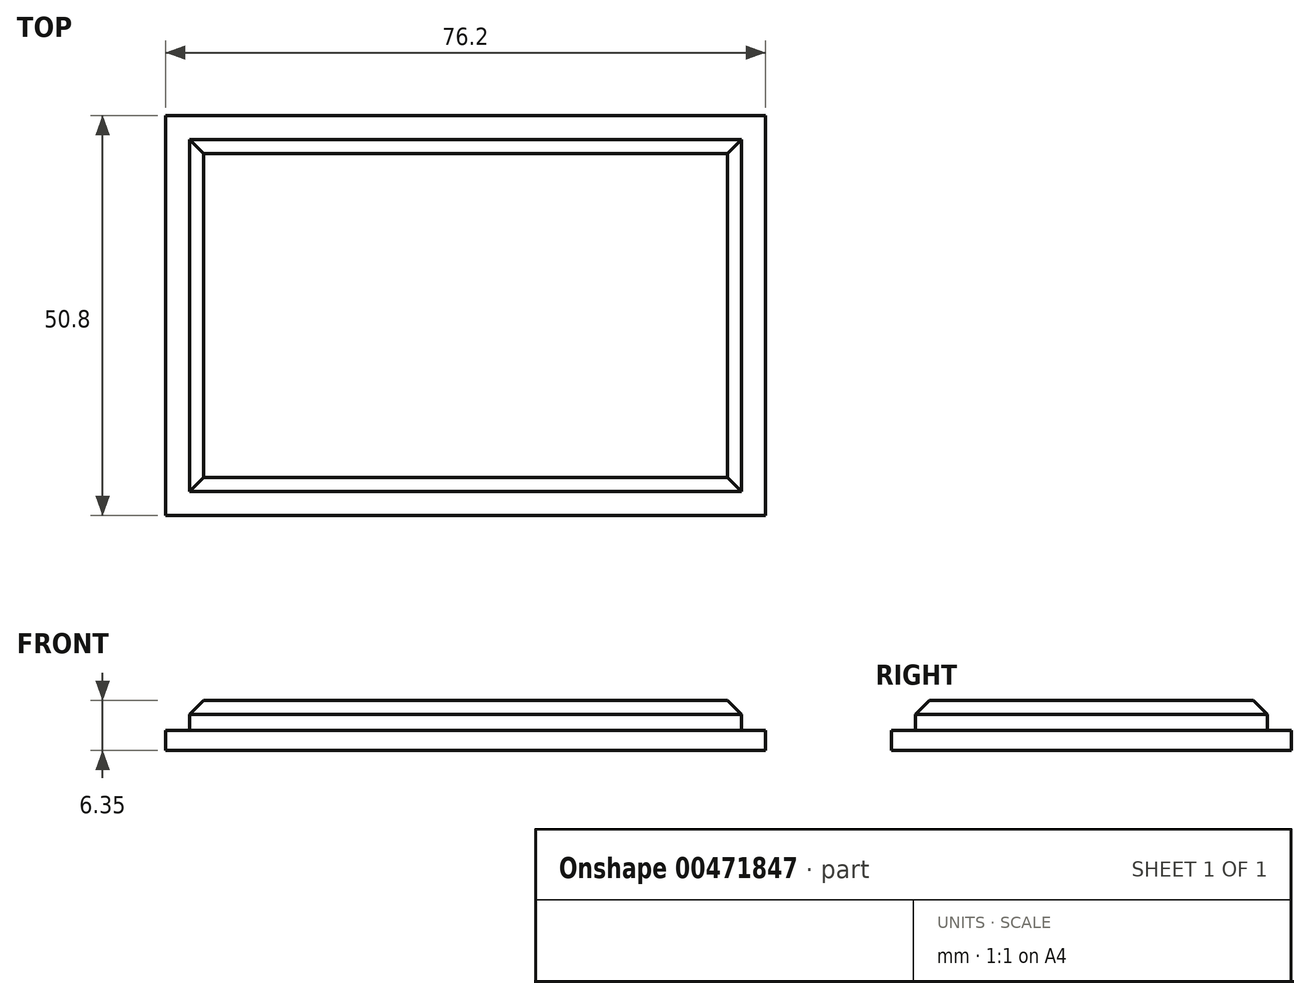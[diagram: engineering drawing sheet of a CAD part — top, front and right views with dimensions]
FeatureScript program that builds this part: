
annotation { "Feature Type Name" : "Feature", "Feature Type Description" : "" }
export const myFeature = defineFeature(function(context is Context, id is Id, definition is map)
    precondition{}
    {
        {
            var Q0;
            Q0=qCreatedBy(makeId("Top.planeOp"),FACE);
            var sketch = newSketch(context, id + "F0", { "sketchPlane" : qUnion([Q0])});
            skLineSegment(sketch, "E0.bottom", {"start": v(-35.2, 23.13) * mm, "end": v(41, 23.13) * mm});
            skLineSegment(sketch, "E0.top", {"start": v(-35.2, -27.67) * mm, "end": v(41, -27.67) * mm});
            skLineSegment(sketch, "E0.left", {"start": v(-35.2, 23.13) * mm, "end": v(-35.2, -27.67) * mm});
            skLineSegment(sketch, "E0.right", {"start": v(41, 23.13) * mm, "end": v(41, -27.67) * mm});
            skSolve(sketch);
        }
        {
            var Q0;
            Q0 = qSketchRegion(id + "F0", true);
            extrude(context, id + "F1", {"entities" : qUnion([Q0]), "depth" : 2.54 * mm});
        }
        {
            var Q0;
            Q0=makeQuery(id+"F1.opExtrude","CAP_FACE",FACE,{"disambiguationData":[OSD([sQuery(id+"F0.wireOp",EDGE,"E0.bottom"),sQuery(id+"F0.wireOp",EDGE,"E0.top"),sQuery(id+"F0.wireOp",EDGE,"E0.left"),sQuery(id+"F0.wireOp",EDGE,"E0.right")])],"isStart":false});
            var sketch = newSketch(context, id + "F2", { "sketchPlane" : qUnion([Q0])});
            skLineSegment(sketch, "E1.bottom", {"start": v(-32.15, 20.08) * mm, "end": v(37.96, 20.08) * mm});
            skLineSegment(sketch, "E1.top", {"start": v(-32.15, -24.62) * mm, "end": v(37.96, -24.62) * mm});
            skLineSegment(sketch, "E1.left", {"start": v(-32.15, 20.08) * mm, "end": v(-32.15, -24.62) * mm});
            skLineSegment(sketch, "E1.right", {"start": v(37.96, 20.08) * mm, "end": v(37.96, -24.62) * mm});
            skLineSegment(sketch, "E2", {"start": v(37.96, 4.33) * mm, "end": v(41, 4.33) * mm});
            skLineSegment(sketch, "E3", {"start": v(-32.15, -24.62) * mm, "end": v(-32.15, -27.67) * mm});
            skSolve(sketch);
        }
        {
            var Q0;
            {var subQ1=sQuery(id+"F2.wireOp",EDGE,"E1.bottom");Q0=makeQuery(id+"F2.imprint","IMPRINT",FACE,{"disambiguationData":[TD([[makeQuery(id+"F2.imprint","IMPRINT",EDGE,{"derivedFrom":subQ1}),-1.0]])]});}
            extrude(context, id + "F3", {"entities" : qUnion([Q0]), "operationType" : NewBodyOperationType.ADD, "depth" : 3.8 * mm});
        }
        {
            var Q0;
            Q0=makeQuery(id+"F3.opExtrude","CAP_EDGE",EDGE,{"disambiguationData":[OSD([sQuery(id+"F2.wireOp",EDGE,"E1.top")])],"isStart":false});
            var Q1;
            Q1=makeQuery(id+"F3.opExtrude","CAP_EDGE",EDGE,{"disambiguationData":[OSD([sQuery(id+"F2.wireOp",EDGE,"E1.left")])],"isStart":false});
            var Q2;
            Q2=makeQuery(id+"F3.opExtrude","CAP_EDGE",EDGE,{"disambiguationData":[OSD([sQuery(id+"F2.wireOp",EDGE,"E1.right")])],"isStart":false});
            var Q3;
            Q3=makeQuery(id+"F3.opExtrude","CAP_EDGE",EDGE,{"disambiguationData":[OSD([sQuery(id+"F2.wireOp",EDGE,"E1.bottom")])],"isStart":false});
            chamfer(context, id + "F4", {"entities" : qUnion([Q0, Q1, Q2, Q3]), "width" : 1.78 * mm, "tangentPropagation" : true});
        }
    });
